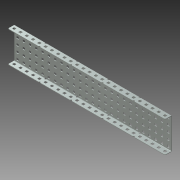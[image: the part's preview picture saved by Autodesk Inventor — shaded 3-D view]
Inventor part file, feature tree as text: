
AUTODESK INVENTOR PART (.ipt)
format: ipt  version: 2013 (Build 170138000, 138)  size: 3,572,224 bytes
history: native  units: mm (DEFAULTED — no unit token found)
features: other x175, extrude x175, pattern_linear x2, sketch x2, imported_body x1, plane x1, mirror x1
ambient origin geometry x8: Origin, YZ Plane, XZ Plane, XY Plane, X Axis, Y Axis, Z Axis, Center Point
bodies: Solid1 (feature_tree)
feature tree (357):
  imported_body  "Base1"
  pattern_linear  "Rectangular Pattern1"  Count1=25  [1 undecoded]
  pattern_linear  "Rectangular Pattern2"  Spacing1=12.7mm  [1 undecoded]
  plane  "Work Plane1"
  mirror  "Mirror1"
  sketch  "Sketch1"  dims[d1=1.1684mm]
  other  "Srf1"
  other  "Srf2"
  other  "Srf3"
  other  "Srf4"
  other  "Srf5"
  other  "Srf6"
  other  "Srf7"
  other  "Srf8"
  other  "Srf9"
  other  "Srf10"
  other  "Srf11"
  other  "Srf12"
  other  "Srf13"
  other  "Srf14"
  other  "Srf15"
  other  "Srf16"
  other  "Srf17"
  other  "Srf18"
  other  "Srf19"
  other  "Srf20"
  other  "Srf21"
  other  "Srf22"
  other  "Srf23"
  other  "Srf24"
  other  "Srf25"
  other  "Srf26"
  other  "Srf27"
  other  "Srf28"
  other  "Srf29"
  other  "Srf30"
  other  "Srf31"
  other  "Srf32"
  other  "Srf33"
  other  "Srf34"
  other  "Srf35"
  other  "Srf36"
  other  "Srf37"
  other  "Srf38"
  other  "Srf39"
  other  "Srf40"
  other  "Srf41"
  other  "Srf42"
  other  "Srf43"
  other  "Srf44"
  other  "Srf45"
  other  "Srf46"
  other  "Srf47"
  other  "Srf48"
  other  "Srf49"
  other  "Srf50"
  other  "Srf51"
  other  "Srf52"
  other  "Srf53"
  other  "Srf54"
  other  "Srf55"
  other  "Srf56"
  other  "Srf57"
  other  "Srf58"
  other  "Srf59"
  other  "Srf60"
  other  "Srf61"
  other  "Srf62"
  other  "Srf63"
  other  "Srf64"
  other  "Srf65"
  other  "Srf66"
  other  "Srf67"
  other  "Srf68"
  other  "Srf69"
  other  "Srf70"
  other  "Srf71"
  other  "Srf72"
  other  "Srf73"
  other  "Srf74"
  other  "Srf75"
  other  "Srf76"
  other  "Srf77"
  other  "Srf78"
  other  "Srf79"
  other  "Srf80"
  other  "Srf81"
  other  "Srf82"
  other  "Srf83"
  other  "Srf84"
  other  "Srf85"
  other  "Srf86"
  other  "Srf87"
  other  "Srf88"
  other  "Srf89"
  other  "Srf90"
  other  "Srf91"
  other  "Srf92"
  other  "Srf93"
  other  "Srf94"
  other  "Srf95"
  other  "Srf96"
  other  "Srf97"
  other  "Srf98"
  other  "Srf99"
  other  "Srf100"
  other  "Srf101"
  other  "Srf102"
  other  "Srf103"
  other  "Srf104"
  other  "Srf105"
  other  "Srf106"
  other  "Srf107"
  other  "Srf108"
  other  "Srf109"
  other  "Srf110"
  other  "Srf111"
  other  "Srf112"
  other  "Srf113"
  other  "Srf114"
  other  "Srf115"
  other  "Srf116"
  other  "Srf117"
  other  "Srf118"
  other  "Srf119"
  other  "Srf120"
  other  "Srf121"
  other  "Srf122"
  other  "Srf123"
  other  "Srf124"
  other  "Srf125"
  sketch  "Sketch2"  dims[d2=0.0mm d3=250.0mm d5=12.7mm d6=50.0mm d8=12.7mm d9=1.1684mm d10=0.0mm d11=250.0mm d13=12.7mm d14=0.0mm d15=0.0mm d16=0.0mm d17=0.0mm d18=0.0mm d19=0.0mm d20=0.0mm d21=0.0mm d22=0.0mm d23=0.0mm d24=0.0mm d25=0.0mm d26=0.0mm d27=0.0mm d28=0.0mm d29=0.0mm d30=0.0mm d31=0.0mm d32=0.0mm d33=0.0mm d34=0.0mm d35=0.0mm d36=0.0mm d37=0.0mm d38=0.0mm d39=0.0mm d40=0.0mm d41=0.0mm d42=0.0mm d43=0.0mm d44=0.0mm d45=0.0mm d46=0.0mm d47=0.0mm d48=0.0mm d49=0.0mm d50=0.0mm d51=0.0mm d52=0.0mm d53=0.0mm d54=0.0mm d55=0.0mm d56=0.0mm d57=0.0mm d58=0.0mm d59=0.0mm d60=0.0mm d61=0.0mm d62=0.0mm d63=0.0mm d64=0.0mm d65=0.0mm d66=0.0mm d67=0.0mm d68=0.0mm d69=0.0mm d70=0.0mm d71=0.0mm d72=0.0mm d73=0.0mm d74=0.0mm d75=0.0mm d76=0.0mm d77=0.0mm d78=0.0mm d79=0.0mm d80=0.0mm d81=0.0mm d82=0.0mm d83=0.0mm d84=0.0mm d85=0.0mm d86=0.0mm d87=0.0mm d88=0.0mm d89=0.0mm d90=0.0mm d91=0.0mm d92=0.0mm d93=0.0mm d94=0.0mm d95=0.0mm d96=0.0mm d97=0.0mm d98=0.0mm d99=0.0mm d100=0.0mm d101=0.0mm d102=0.0mm d103=0.0mm d104=0.0mm d105=0.0mm d106=0.0mm d107=0.0mm d108=0.0mm d109=0.0mm d110=0.0mm d111=0.0mm d112=0.0mm d113=0.0mm d114=0.0mm d115=0.0mm d116=0.0mm d117=0.0mm d118=0.0mm d119=0.0mm d120=0.0mm d121=0.0mm d122=0.0mm d123=0.0mm d124=0.0mm d125=0.0mm d126=0.0mm d127=0.0mm d128=0.0mm d129=0.0mm d130=0.0mm d131=0.0mm d132=0.0mm d133=0.0mm d134=0.0mm d135=0.0mm d136=0.0mm d137=0.0mm d138=0.0mm d139=0.0mm d140=0.0mm d141=0.0mm d142=0.0mm d143=0.0mm d144=0.0mm d145=0.0mm d146=0.0mm d147=0.0mm d148=0.0mm d149=0.0mm d150=0.0mm d151=0.0mm d152=0.0mm d153=0.0mm d154=0.0mm d155=0.0mm d156=0.0mm d157=0.0mm d158=0.0mm d159=0.0mm d160=0.0mm d161=0.0mm d162=0.0mm d163=0.0mm d164=0.0mm d165=0.0mm d166=0.0mm d167=0.0mm d168=0.0mm d169=0.0mm d170=0.0mm d171=0.0mm d172=0.0mm d173=0.0mm d174=0.0mm d175=0.0mm d176=0.0mm d177=0.0mm d178=0.0mm d179=0.0mm d180=0.0mm d181=0.0mm d182=0.0mm d183=0.0mm d184=0.0mm d185=0.0mm d186=0.0mm d187=0.0mm d188=0.0mm d189=0.0mm d190=0.0mm d191=0.0mm d192=0.0mm d193=0.0mm d194=0.0mm d195=0.0mm d196=0.0mm d197=0.0mm d198=0.0mm d199=0.0mm d200=0.0mm d201=0.0mm d202=0.0mm d203=0.0mm d204=0.0mm d205=0.0mm d206=0.0mm d207=0.0mm d208=0.0mm d209=0.0mm d210=0.0mm d211=0.0mm d212=0.0mm d213=0.0mm d214=0.0mm d215=0.0mm d216=0.0mm d217=0.0mm d218=0.0mm d219=0.0mm d220=0.0mm d221=0.0mm d222=0.0mm d223=0.0mm d224=0.0mm d225=0.0mm d226=0.0mm d227=0.0mm d228=0.0mm d229=0.0mm d230=0.0mm d231=0.0mm d232=0.0mm d233=0.0mm d234=0.0mm d235=0.0mm d236=0.0mm d237=0.0mm d238=0.0mm d239=0.0mm d240=0.0mm d241=0.0mm d242=0.0mm d243=0.0mm d244=0.0mm d245=0.0mm d246=0.0mm d247=0.0mm d248=0.0mm d249=0.0mm d250=0.0mm d251=0.0mm d252=0.0mm d253=0.0mm d254=0.0mm d255=0.0mm d256=0.0mm d257=0.0mm d258=0.0mm d259=0.0mm d260=0.0mm d261=0.0mm d262=0.0mm d263=0.0mm d264=0.0mm d265=0.0mm d266=0.0mm d267=0.0mm d268=0.0mm d269=0.0mm d270=0.0mm d271=0.0mm d272=0.0mm d273=0.0mm d274=0.0mm d275=0.0mm d276=0.0mm d277=0.0mm d278=0.0mm d279=0.0mm d280=0.0mm d281=0.0mm d282=0.0mm d283=0.0mm d284=0.0mm d285=0.0mm d286=0.0mm d287=0.0mm d288=0.0mm d289=0.0mm d290=0.0mm d291=0.0mm d292=0.0mm d293=0.0mm d294=0.0mm d295=0.0mm d296=0.0mm d297=0.0mm d298=0.0mm d299=0.0mm d300=0.0mm d301=0.0mm d302=0.0mm d303=0.0mm d304=0.0mm d305=0.0mm d306=0.0mm d307=0.0mm d308=0.0mm d309=0.0mm d310=0.0mm d311=0.0mm d312=0.0mm d313=0.0mm d314=0.0mm d315=0.0mm d316=0.0mm d317=0.0mm d318=0.0mm d319=0.0mm d320=0.0mm d321=0.0mm d322=0.0mm d323=0.0mm d324=0.0mm d325=0.0mm d326=0.0mm d327=0.0mm d328=0.0mm d329=0.0mm d330=0.0mm d331=0.0mm d332=0.0mm d333=0.0mm d334=0.0mm d335=0.0mm d336=0.0mm d337=0.0mm d338=0.0mm d339=0.0mm d340=0.0mm d341=0.0mm d342=0.0mm d343=0.0mm d344=0.0mm d345=0.0mm d346=0.0mm d347=0.0mm d348=0.0mm d349=0.0mm d350=0.0mm d351=0.0mm d352=0.0mm d353=0.0mm d354=0.0mm d355=0.0mm d356=0.0mm d357=0.0mm d358=0.0mm d359=0.0mm d360=0.0mm d361=0.0mm d362=0.0mm d363=0.0mm]
  other  "Srf126"
  other  "Srf127"
  other  "Srf128"
  other  "Srf129"
  other  "Srf130"
  other  "Srf131"
  other  "Srf132"
  other  "Srf133"
  other  "Srf134"
  other  "Srf135"
  other  "Srf136"
  other  "Srf137"
  other  "Srf138"
  other  "Srf139"
  other  "Srf140"
  other  "Srf141"
  other  "Srf142"
  other  "Srf143"
  other  "Srf144"
  other  "Srf145"
  other  "Srf146"
  other  "Srf147"
  other  "Srf148"
  other  "Srf149"
  other  "Srf150"
  other  "Srf175"
  other  "Srf151"
  other  "Srf152"
  other  "Srf153"
  other  "Srf154"
  other  "Srf155"
  other  "Srf156"
  other  "Srf157"
  other  "Srf158"
  other  "Srf159"
  other  "Srf160"
  other  "Srf161"
  other  "Srf162"
  other  "Srf163"
  other  "Srf164"
  other  "Srf165"
  other  "Srf166"
  other  "Srf167"
  other  "Srf168"
  other  "Srf169"
  other  "Srf170"
  other  "Srf171"
  other  "Srf172"
  other  "Srf173"
  other  "Srf174"
  extrude  "ExtrusionSrf1"  Depth=50.0mm
  extrude  "ExtrusionSrf126"  Depth=1.1684mm
  extrude  "ExtrusionSrf2"  TaperAngle=0.0deg  [1 undecoded]
  extrude  "ExtrusionSrf3"  Depth=250.0mm
  extrude  "ExtrusionSrf4"  Depth=12.7mm
  extrude  "ExtrusionSrf5"  TaperAngle=0.0deg  [1 undecoded]
  extrude  "ExtrusionSrf6"  TaperAngle=0.0deg  [1 undecoded]
  extrude  "ExtrusionSrf7"  TaperAngle=0.0deg  [1 undecoded]
  extrude  "ExtrusionSrf8"  TaperAngle=0.0deg  [1 undecoded]
  extrude  "ExtrusionSrf9"  TaperAngle=0.0deg  [1 undecoded]
  extrude  "ExtrusionSrf10"  TaperAngle=0.0deg  [1 undecoded]
  extrude  "ExtrusionSrf11"  TaperAngle=0.0deg  [1 undecoded]
  extrude  "ExtrusionSrf12"  TaperAngle=0.0deg  [1 undecoded]
  extrude  "ExtrusionSrf13"  TaperAngle=0.0deg  [1 undecoded]
  extrude  "ExtrusionSrf14"  TaperAngle=0.0deg  [1 undecoded]
  extrude  "ExtrusionSrf15"  TaperAngle=0.0deg  [1 undecoded]
  extrude  "ExtrusionSrf16"  TaperAngle=0.0deg  [1 undecoded]
  extrude  "ExtrusionSrf17"  TaperAngle=0.0deg  [1 undecoded]
  extrude  "ExtrusionSrf18"  TaperAngle=0.0deg  [1 undecoded]
  extrude  "ExtrusionSrf19"  TaperAngle=0.0deg  [1 undecoded]
  extrude  "ExtrusionSrf20"  TaperAngle=0.0deg  [1 undecoded]
  extrude  "ExtrusionSrf21"  TaperAngle=0.0deg  [1 undecoded]
  extrude  "ExtrusionSrf22"  TaperAngle=0.0deg  [1 undecoded]
  extrude  "ExtrusionSrf23"  TaperAngle=0.0deg  [1 undecoded]
  extrude  "ExtrusionSrf24"  TaperAngle=0.0deg  [1 undecoded]
  extrude  "ExtrusionSrf25"  TaperAngle=0.0deg  [1 undecoded]
  extrude  "ExtrusionSrf26"  TaperAngle=0.0deg  [1 undecoded]
  extrude  "ExtrusionSrf27"  TaperAngle=0.0deg  [1 undecoded]
  extrude  "ExtrusionSrf28"  TaperAngle=0.0deg  [1 undecoded]
  extrude  "ExtrusionSrf29"  TaperAngle=0.0deg  [1 undecoded]
  extrude  "ExtrusionSrf30"  TaperAngle=0.0deg  [1 undecoded]
  extrude  "ExtrusionSrf31"  TaperAngle=0.0deg  [1 undecoded]
  extrude  "ExtrusionSrf32"  TaperAngle=0.0deg  [1 undecoded]
  extrude  "ExtrusionSrf33"  TaperAngle=0.0deg  [1 undecoded]
  extrude  "ExtrusionSrf34"  TaperAngle=0.0deg  [1 undecoded]
  extrude  "ExtrusionSrf35"  TaperAngle=0.0deg  [1 undecoded]
  extrude  "ExtrusionSrf36"  TaperAngle=0.0deg  [1 undecoded]
  extrude  "ExtrusionSrf37"  TaperAngle=0.0deg  [1 undecoded]
  extrude  "ExtrusionSrf38"  TaperAngle=0.0deg  [1 undecoded]
  extrude  "ExtrusionSrf39"  TaperAngle=0.0deg  [1 undecoded]
  extrude  "ExtrusionSrf40"  TaperAngle=0.0deg  [1 undecoded]
  extrude  "ExtrusionSrf41"  TaperAngle=0.0deg  [1 undecoded]
  extrude  "ExtrusionSrf42"  TaperAngle=0.0deg  [1 undecoded]
  extrude  "ExtrusionSrf43"  TaperAngle=0.0deg  [1 undecoded]
  extrude  "ExtrusionSrf44"  TaperAngle=0.0deg  [1 undecoded]
  extrude  "ExtrusionSrf45"  TaperAngle=0.0deg  [1 undecoded]
  extrude  "ExtrusionSrf46"  TaperAngle=0.0deg  [1 undecoded]
  extrude  "ExtrusionSrf47"  TaperAngle=0.0deg  [1 undecoded]
  extrude  "ExtrusionSrf48"  TaperAngle=0.0deg  [1 undecoded]
  extrude  "ExtrusionSrf49"  TaperAngle=0.0deg  [1 undecoded]
  extrude  "ExtrusionSrf50"  TaperAngle=0.0deg  [1 undecoded]
  extrude  "ExtrusionSrf51"  TaperAngle=0.0deg  [1 undecoded]
  extrude  "ExtrusionSrf52"  TaperAngle=0.0deg  [1 undecoded]
  extrude  "ExtrusionSrf53"  TaperAngle=0.0deg  [1 undecoded]
  extrude  "ExtrusionSrf54"  TaperAngle=0.0deg  [1 undecoded]
  extrude  "ExtrusionSrf55"  TaperAngle=0.0deg  [1 undecoded]
  extrude  "ExtrusionSrf56"  TaperAngle=0.0deg  [1 undecoded]
  extrude  "ExtrusionSrf57"  TaperAngle=0.0deg  [1 undecoded]
  extrude  "ExtrusionSrf58"  TaperAngle=0.0deg  [1 undecoded]
  extrude  "ExtrusionSrf59"  TaperAngle=0.0deg  [1 undecoded]
  extrude  "ExtrusionSrf60"  TaperAngle=0.0deg  [1 undecoded]
  extrude  "ExtrusionSrf61"  TaperAngle=0.0deg  [1 undecoded]
  extrude  "ExtrusionSrf62"  TaperAngle=0.0deg  [1 undecoded]
  extrude  "ExtrusionSrf63"  TaperAngle=0.0deg  [1 undecoded]
  extrude  "ExtrusionSrf64"  TaperAngle=0.0deg  [1 undecoded]
  extrude  "ExtrusionSrf65"  TaperAngle=0.0deg  [1 undecoded]
  extrude  "ExtrusionSrf66"  TaperAngle=0.0deg  [1 undecoded]
  extrude  "ExtrusionSrf67"  TaperAngle=0.0deg  [1 undecoded]
  extrude  "ExtrusionSrf68"  TaperAngle=0.0deg  [1 undecoded]
  extrude  "ExtrusionSrf69"  TaperAngle=0.0deg  [1 undecoded]
  extrude  "ExtrusionSrf70"  TaperAngle=0.0deg  [1 undecoded]
  extrude  "ExtrusionSrf71"  TaperAngle=0.0deg  [1 undecoded]
  extrude  "ExtrusionSrf72"  TaperAngle=0.0deg  [1 undecoded]
  extrude  "ExtrusionSrf73"  TaperAngle=0.0deg  [1 undecoded]
  extrude  "ExtrusionSrf74"  TaperAngle=0.0deg  [1 undecoded]
  extrude  "ExtrusionSrf75"  TaperAngle=0.0deg  [1 undecoded]
  extrude  "ExtrusionSrf76"  TaperAngle=0.0deg  [1 undecoded]
  extrude  "ExtrusionSrf77"  TaperAngle=0.0deg  [1 undecoded]
  extrude  "ExtrusionSrf78"  TaperAngle=0.0deg  [1 undecoded]
  extrude  "ExtrusionSrf79"  TaperAngle=0.0deg  [1 undecoded]
  extrude  "ExtrusionSrf80"  TaperAngle=0.0deg  [1 undecoded]
  extrude  "ExtrusionSrf81"  TaperAngle=0.0deg  [1 undecoded]
  extrude  "ExtrusionSrf82"  TaperAngle=0.0deg  [1 undecoded]
  extrude  "ExtrusionSrf83"  TaperAngle=0.0deg  [1 undecoded]
  extrude  "ExtrusionSrf84"  TaperAngle=0.0deg  [1 undecoded]
  extrude  "ExtrusionSrf85"  TaperAngle=0.0deg  [1 undecoded]
  extrude  "ExtrusionSrf86"  TaperAngle=0.0deg  [1 undecoded]
  extrude  "ExtrusionSrf87"  TaperAngle=0.0deg  [1 undecoded]
  extrude  "ExtrusionSrf88"  TaperAngle=0.0deg  [1 undecoded]
  extrude  "ExtrusionSrf89"  TaperAngle=0.0deg  [1 undecoded]
  extrude  "ExtrusionSrf90"  TaperAngle=0.0deg  [1 undecoded]
  extrude  "ExtrusionSrf91"  TaperAngle=0.0deg  [1 undecoded]
  extrude  "ExtrusionSrf92"  TaperAngle=0.0deg  [1 undecoded]
  extrude  "ExtrusionSrf93"  TaperAngle=0.0deg  [1 undecoded]
  extrude  "ExtrusionSrf94"  TaperAngle=0.0deg  [1 undecoded]
  extrude  "ExtrusionSrf95"  TaperAngle=0.0deg  [1 undecoded]
  extrude  "ExtrusionSrf96"  TaperAngle=0.0deg  [1 undecoded]
  extrude  "ExtrusionSrf97"  TaperAngle=0.0deg  [1 undecoded]
  extrude  "ExtrusionSrf98"  TaperAngle=0.0deg  [1 undecoded]
  extrude  "ExtrusionSrf99"  TaperAngle=0.0deg  [1 undecoded]
  extrude  "ExtrusionSrf100"  TaperAngle=0.0deg  [1 undecoded]
  extrude  "ExtrusionSrf101"  TaperAngle=0.0deg  [1 undecoded]
  extrude  "ExtrusionSrf102"  TaperAngle=0.0deg  [1 undecoded]
  extrude  "ExtrusionSrf103"  TaperAngle=0.0deg  [1 undecoded]
  extrude  "ExtrusionSrf104"  TaperAngle=0.0deg  [1 undecoded]
  extrude  "ExtrusionSrf105"  TaperAngle=0.0deg  [1 undecoded]
  extrude  "ExtrusionSrf106"  TaperAngle=0.0deg  [1 undecoded]
  extrude  "ExtrusionSrf107"  TaperAngle=0.0deg  [1 undecoded]
  extrude  "ExtrusionSrf108"  TaperAngle=0.0deg  [1 undecoded]
  extrude  "ExtrusionSrf109"  TaperAngle=0.0deg  [1 undecoded]
  extrude  "ExtrusionSrf110"  TaperAngle=0.0deg  [1 undecoded]
  extrude  "ExtrusionSrf111"  TaperAngle=0.0deg  [1 undecoded]
  extrude  "ExtrusionSrf112"  TaperAngle=0.0deg  [1 undecoded]
  extrude  "ExtrusionSrf113"  TaperAngle=0.0deg  [1 undecoded]
  extrude  "ExtrusionSrf114"  TaperAngle=0.0deg  [1 undecoded]
  extrude  "ExtrusionSrf115"  TaperAngle=0.0deg  [1 undecoded]
  extrude  "ExtrusionSrf116"  TaperAngle=0.0deg  [1 undecoded]
  extrude  "ExtrusionSrf117"  TaperAngle=0.0deg  [1 undecoded]
  extrude  "ExtrusionSrf118"  TaperAngle=0.0deg  [1 undecoded]
  extrude  "ExtrusionSrf119"  TaperAngle=0.0deg  [1 undecoded]
  extrude  "ExtrusionSrf120"  TaperAngle=0.0deg  [1 undecoded]
  extrude  "ExtrusionSrf121"  TaperAngle=0.0deg  [1 undecoded]
  extrude  "ExtrusionSrf122"  TaperAngle=0.0deg  [1 undecoded]
  extrude  "ExtrusionSrf123"  TaperAngle=0.0deg  [1 undecoded]
  extrude  "ExtrusionSrf124"  TaperAngle=0.0deg  [1 undecoded]
  extrude  "ExtrusionSrf125"  TaperAngle=0.0deg  [1 undecoded]
  extrude  "ExtrusionSrf127"  TaperAngle=0.0deg  [1 undecoded]
  extrude  "ExtrusionSrf128"  TaperAngle=0.0deg  [1 undecoded]
  extrude  "ExtrusionSrf129"  TaperAngle=0.0deg  [1 undecoded]
  extrude  "ExtrusionSrf130"  TaperAngle=0.0deg  [1 undecoded]
  extrude  "ExtrusionSrf131"  TaperAngle=0.0deg  [1 undecoded]
  extrude  "ExtrusionSrf132"  TaperAngle=0.0deg  [1 undecoded]
  extrude  "ExtrusionSrf133"  TaperAngle=0.0deg  [1 undecoded]
  extrude  "ExtrusionSrf134"  TaperAngle=0.0deg  [1 undecoded]
  extrude  "ExtrusionSrf135"  TaperAngle=0.0deg  [1 undecoded]
  extrude  "ExtrusionSrf136"  TaperAngle=0.0deg  [1 undecoded]
  extrude  "ExtrusionSrf137"  TaperAngle=0.0deg  [1 undecoded]
  extrude  "ExtrusionSrf138"  TaperAngle=0.0deg  [1 undecoded]
  extrude  "ExtrusionSrf139"  TaperAngle=0.0deg  [1 undecoded]
  extrude  "ExtrusionSrf140"  TaperAngle=0.0deg  [1 undecoded]
  extrude  "ExtrusionSrf141"  TaperAngle=0.0deg  [1 undecoded]
  extrude  "ExtrusionSrf142"  TaperAngle=0.0deg  [1 undecoded]
  extrude  "ExtrusionSrf143"  TaperAngle=0.0deg  [1 undecoded]
  extrude  "ExtrusionSrf144"  TaperAngle=0.0deg  [1 undecoded]
  extrude  "ExtrusionSrf145"  TaperAngle=0.0deg  [1 undecoded]
  extrude  "ExtrusionSrf146"  TaperAngle=0.0deg  [1 undecoded]
  extrude  "ExtrusionSrf147"  TaperAngle=0.0deg  [1 undecoded]
  extrude  "ExtrusionSrf148"  TaperAngle=0.0deg  [1 undecoded]
  extrude  "ExtrusionSrf149"  TaperAngle=0.0deg  [1 undecoded]
  extrude  "ExtrusionSrf150"  TaperAngle=0.0deg  [1 undecoded]
  extrude  "ExtrusionSrf151"  TaperAngle=0.0deg  [1 undecoded]
  extrude  "ExtrusionSrf152"  TaperAngle=0.0deg  [1 undecoded]
  extrude  "ExtrusionSrf153"  TaperAngle=0.0deg  [1 undecoded]
  extrude  "ExtrusionSrf154"  TaperAngle=0.0deg  [1 undecoded]
  extrude  "ExtrusionSrf155"  TaperAngle=0.0deg  [1 undecoded]
  extrude  "ExtrusionSrf156"  TaperAngle=0.0deg  [1 undecoded]
  extrude  "ExtrusionSrf157"  TaperAngle=0.0deg  [1 undecoded]
  extrude  "ExtrusionSrf158"  TaperAngle=0.0deg  [1 undecoded]
  extrude  "ExtrusionSrf159"  TaperAngle=0.0deg  [1 undecoded]
  extrude  "ExtrusionSrf160"  TaperAngle=0.0deg  [1 undecoded]
  extrude  "ExtrusionSrf161"  TaperAngle=0.0deg  [1 undecoded]
  extrude  "ExtrusionSrf162"  TaperAngle=0.0deg  [1 undecoded]
  extrude  "ExtrusionSrf163"  TaperAngle=0.0deg  [1 undecoded]
  extrude  "ExtrusionSrf164"  TaperAngle=0.0deg  [1 undecoded]
  extrude  "ExtrusionSrf165"  TaperAngle=0.0deg  [1 undecoded]
  extrude  "ExtrusionSrf166"  TaperAngle=0.0deg  [1 undecoded]
  extrude  "ExtrusionSrf167"  TaperAngle=0.0deg  [1 undecoded]
  extrude  "ExtrusionSrf168"  TaperAngle=0.0deg  [1 undecoded]
  extrude  "ExtrusionSrf169"  TaperAngle=0.0deg  [1 undecoded]
  extrude  "ExtrusionSrf170"  TaperAngle=0.0deg  [1 undecoded]
  extrude  "ExtrusionSrf171"  TaperAngle=0.0deg  [1 undecoded]
  extrude  "ExtrusionSrf172"  TaperAngle=0.0deg  [1 undecoded]
  extrude  "ExtrusionSrf173"  TaperAngle=0.0deg  [1 undecoded]
  extrude  "ExtrusionSrf174"  TaperAngle=0.0deg  [1 undecoded]
  extrude  "ExtrusionSrf175"  TaperAngle=0.0deg  [1 undecoded]
note: 173 required parameter values undecoded (feature->parameter linkage not recoverable at this tier; creation-order binding heuristic only, values carry confidence <= 0.55)
